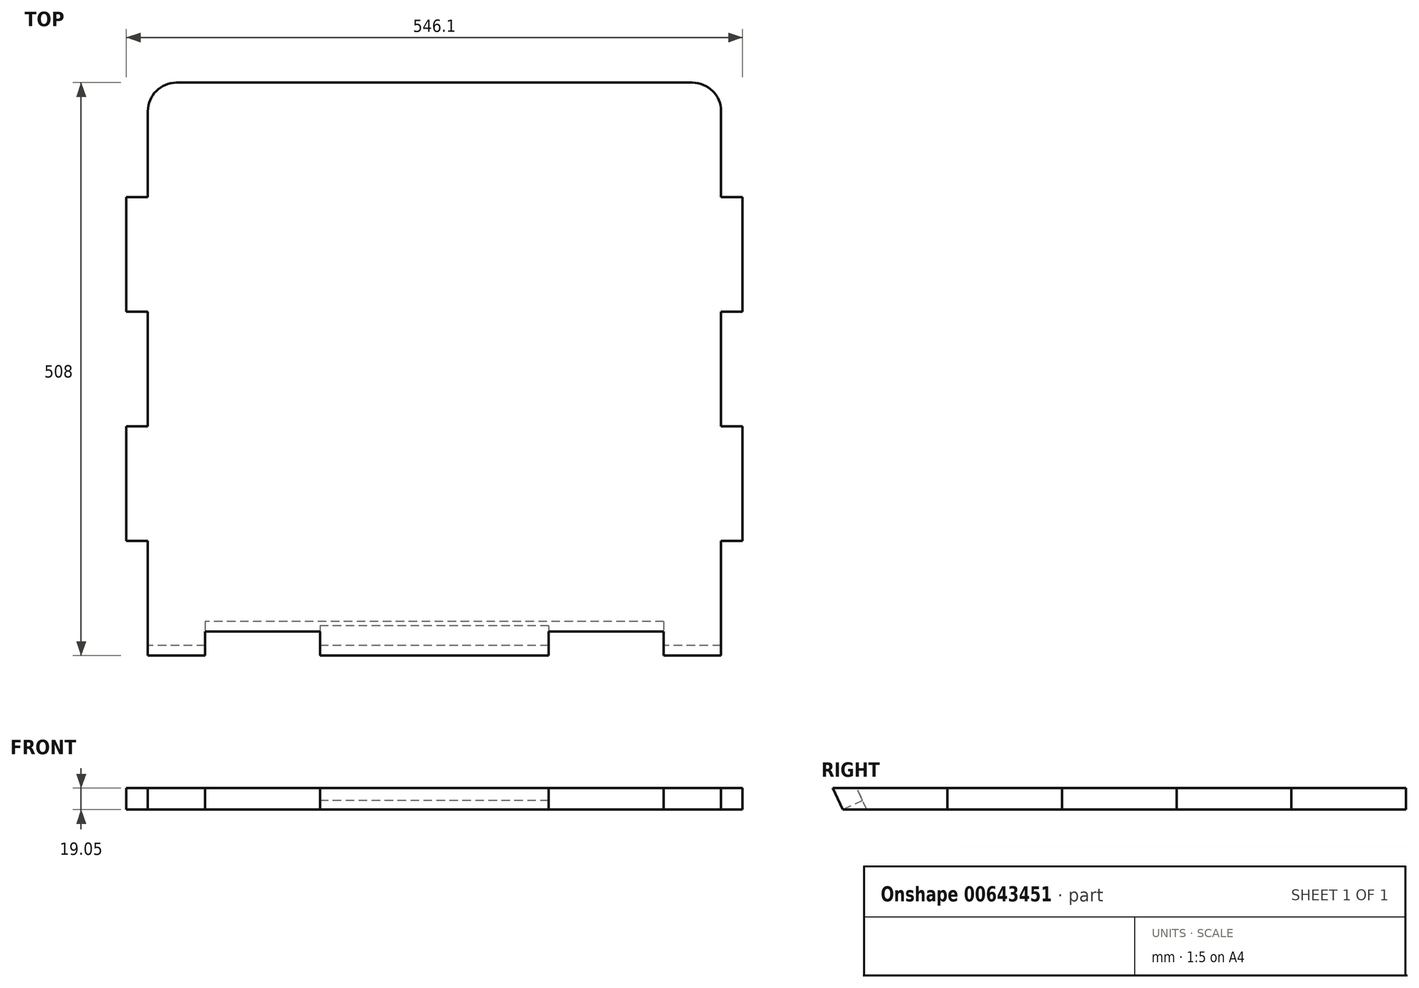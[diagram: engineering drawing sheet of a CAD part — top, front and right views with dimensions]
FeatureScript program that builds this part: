
annotation { "Feature Type Name" : "Feature", "Feature Type Description" : "" }
export const myFeature = defineFeature(function(context is Context, id is Id, definition is map)
    precondition{}
    {
        {
            var Q0;
            Q0=qCreatedBy(makeId("Top.planeOp"),FACE);
            var sketch = newSketch(context, id + "F0", { "sketchPlane" : qUnion([Q0])});
            skLineSegment(sketch, "E0", {"start": v(0, 0) * mm, "end": v(508, 0) * mm});
            skLineSegment(sketch, "E1", {"start": v(254, 0) * mm, "end": v(254, 508) * mm, "construction": true});
            skLineSegment(sketch, "E2", {"start": v(0, 0) * mm, "end": v(0, 101.6) * mm});
            skLineSegment(sketch, "E3", {"start": v(508, 0) * mm, "end": v(508, 101.6) * mm});
            skLineSegment(sketch, "E4", {"start": v(254, 508) * mm, "end": v(508, 508) * mm});
            skLineSegment(sketch, "E5", {"start": v(254, 508) * mm, "end": v(0, 508) * mm});
            skLineSegment(sketch, "E6", {"start": v(254, 254) * mm, "end": v(508, 254) * mm, "construction": true});
            skPoint(sketch, "E6.endSnap0", {"position": v(508, 254) * mm});
            skLineSegment(sketch, "E7", {"start": v(527.05, 355.6) * mm, "end": v(527.05, 406.4) * mm});
            skLineSegment(sketch, "E8", {"start": v(527.05, 406.4) * mm, "end": v(508, 406.4) * mm});
            skLineSegment(sketch, "E9.trimOffspring", {"start": v(508, 406.4) * mm, "end": v(508, 508) * mm});
            skLineSegment(sketch, "E10.MirrorCS", {"start": v(527.05, 355.6) * mm, "end": v(527.05, 304.8) * mm});
            skLineSegment(sketch, "E11.MirrorCS", {"start": v(527.05, 304.8) * mm, "end": v(508, 304.8) * mm});
            skLineSegment(sketch, "E12.MirrorCS", {"start": v(527.05, 101.6) * mm, "end": v(508, 101.6) * mm});
            skLineSegment(sketch, "E13.MirrorCS", {"start": v(527.05, 152.4) * mm, "end": v(527.05, 101.6) * mm});
            skLineSegment(sketch, "E14.MirrorCS", {"start": v(527.05, 152.4) * mm, "end": v(527.05, 203.2) * mm});
            skLineSegment(sketch, "E15.MirrorCS", {"start": v(527.05, 203.2) * mm, "end": v(508, 203.2) * mm});
            skLineSegment(sketch, "E16.trimOffspring", {"start": v(508, 203.2) * mm, "end": v(508, 304.8) * mm});
            skLineSegment(sketch, "E17.MirrorCS", {"start": v(-19.05, 406.4) * mm, "end": v(0, 406.4) * mm});
            skLineSegment(sketch, "E18.MirrorCS", {"start": v(-19.05, 355.6) * mm, "end": v(-19.05, 406.4) * mm});
            skLineSegment(sketch, "E19.MirrorCS", {"start": v(-19.05, 355.6) * mm, "end": v(-19.05, 304.8) * mm});
            skLineSegment(sketch, "E20.MirrorCS", {"start": v(-19.05, 304.8) * mm, "end": v(0, 304.8) * mm});
            skLineSegment(sketch, "E21.MirrorCS", {"start": v(-19.05, 203.2) * mm, "end": v(0, 203.2) * mm});
            skLineSegment(sketch, "E22.MirrorCS", {"start": v(-19.05, 152.4) * mm, "end": v(-19.05, 203.2) * mm});
            skLineSegment(sketch, "E23.MirrorCS", {"start": v(-19.05, 152.4) * mm, "end": v(-19.05, 101.6) * mm});
            skLineSegment(sketch, "E24.MirrorCS", {"start": v(-19.05, 101.6) * mm, "end": v(0, 101.6) * mm});
            skLineSegment(sketch, "E25.trimOffspring", {"start": v(0, 406.4) * mm, "end": v(0, 508) * mm});
            skLineSegment(sketch, "E26.trimOffspring", {"start": v(0, 203.2) * mm, "end": v(0, 304.8) * mm});
            skSolve(sketch);
        }
        {
            var Q0;
            Q0=makeQuery(id+"F0.imprint","IMPRINT",FACE,{"disambiguationData":[TD([[makeQuery(id+"F0.imprint","IMPRINT",EDGE,{"derivedFrom":sQuery(id+"F0.wireOp",EDGE,"E0")}),1.0]])]});
            extrude(context, id + "F1", {"entities" : qUnion([Q0]), "depth" : 19.05 * mm, "offsetDistance" : 25.4 * mm});
        }
        {
            var Q0;
            Q0=makeQuery(id+"F1.opExtrude","SWEPT_EDGE",EDGE,{"disambiguationData":[OSD([sQuery(id+"F0.wireOp",EDGE,"E5"),sQuery(id+"F0.wireOp",EDGE,"E25.trimOffspring")])]});
            var Q1;
            Q1=makeQuery(id+"F1.opExtrude","SWEPT_EDGE",EDGE,{"disambiguationData":[OSD([sQuery(id+"F0.wireOp",EDGE,"E4"),sQuery(id+"F0.wireOp",EDGE,"E9.trimOffspring")])]});
            fillet(context, id + "F2", {"entities" : qUnion([Q0, Q1]), "radius" : 25.4 * mm, "tangentPropagation" : true, "allowEdgeOverflow" : false});
        }
        {
            var Q0;
            Q0=makeQuery(id+"F1.opExtrude","SWEPT_FACE",FACE,{"disambiguationData":[OSD([sQuery(id+"F0.wireOp",EDGE,"E2")])]});
            var sketch = newSketch(context, id + "F3", { "sketchPlane" : qUnion([Q0])});
            skLineSegment(sketch, "E27", {"start": v(0, 19.05) * mm, "end": v(-8.88, 0) * mm});
            skLineSegment(sketch, "E28.0", {"start": v(0, 0) * mm, "end": v(-8.88, 0) * mm});
            skLineSegment(sketch, "E29.0", {"start": v(0, 19.05) * mm, "end": v(0, 0) * mm});
            skPoint(sketch, "E30.orphan", {"position": v(-101.6, 0) * mm});
            skPoint(sketch, "E31.0.end.orphan", {"position": v(-101.6, 19.05) * mm});
            skLineSegment(sketch, "E32.0", {"start": v(0, 19.05) * mm, "end": v(-101.6, 19.05) * mm, "construction": true});
            skSolve(sketch);
        }
        {
            var Q0;
            Q0=makeQuery(id+"F3.imprint","IMPRINT",FACE,{"disambiguationData":[TD([[makeQuery(id+"F3.imprint","IMPRINT",EDGE,{"derivedFrom":sQuery(id+"F3.wireOp",EDGE,"E27")}),1.0]])]});
            extrude(context, id + "F4", {"entities" : qUnion([Q0]), "operationType" : NewBodyOperationType.REMOVE, "endBound" : BoundingType.THROUGH_ALL, "oppositeDirection" : true, "depth" : 25.4 * mm, "offsetDistance" : 25.4 * mm});
        }
        {
            var Q0;
            Q0=makeQuery(id+"F4.boolean.opBoolean","MERGE",EDGE,{"derivedFrom":[makeQuery(id+"F1.opExtrude","CAP_EDGE",EDGE,{"disambiguationData":[OSD([sQuery(id+"F0.wireOp",EDGE,"E0")])],"isStart":false}),makeQuery(id+"F4.opExtrude","SWEPT_EDGE",EDGE,{"disambiguationData":[OSD([sQuery(id+"F0.wireOp",EDGE,"E2"),sQuery(id+"F3.wireOp",EDGE,"E27"),sQuery(id+"F3.wireOp",EDGE,"E29.0")])]})]});
            cPlane(context, id + "F5", {"entities" : qUnion([Q0]), "cplaneType" : CPlaneType.LINE_ANGLE, "offset" : 25.4 * mm, "angle" : 65 * degree, "oppositeDirection" : true, "width" : 152.4 * mm, "height" : 152.4 * mm});
        }
        {
            var Q0;
            Q0=qCreatedBy(id+"F5.planeOp",FACE);
            var sketch = newSketch(context, id + "F6", { "sketchPlane" : qUnion([Q0])});
            skLineSegment(sketch, "E33.0", {"start": v(50.8, -8.05) * mm, "end": v(152.65, -8.05) * mm});
            skLineSegment(sketch, "E34", {"start": v(50.8, -27.33) * mm, "end": v(152.65, -27.33) * mm});
            skLineSegment(sketch, "E35", {"start": v(152.65, -27.33) * mm, "end": v(152.65, -8.05) * mm});
            skLineSegment(sketch, "E36", {"start": v(50.8, -27.33) * mm, "end": v(50.8, -8.05) * mm});
            skLineSegment(sketch, "E37.MirrorCS", {"start": v(355.35, -27.33) * mm, "end": v(355.35, -8.05) * mm});
            skLineSegment(sketch, "E38.MirrorCS", {"start": v(457.2, -27.33) * mm, "end": v(457.2, -8.05) * mm});
            skLineSegment(sketch, "E39.MirrorCS", {"start": v(457.2, -27.33) * mm, "end": v(355.35, -27.33) * mm});
            skPoint(sketch, "E40.start.orphan", {"position": v(0, -8.05) * mm});
            skLineSegment(sketch, "E41.trimOffspring", {"start": v(355.35, -8.05) * mm, "end": v(457.2, -8.05) * mm});
            skPoint(sketch, "E42.orphan", {"position": v(508, -8.05) * mm});
            skPoint(sketch, "E43.start.orphan", {"position": v(254, -8.05) * mm});
            skSolve(sketch);
        }
        {
            var Q0;
            Q0=makeQuery(id+"F6.imprint","IMPRINT",FACE,{"disambiguationData":[TD([[makeQuery(id+"F6.imprint","IMPRINT",EDGE,{"derivedFrom":sQuery(id+"F6.wireOp",EDGE,"E33.0")}),-1.0]])]});
            var Q1;
            Q1=makeQuery(id+"F6.imprint","IMPRINT",FACE,{"disambiguationData":[TD([[makeQuery(id+"F6.imprint","IMPRINT",EDGE,{"derivedFrom":sQuery(id+"F6.wireOp",EDGE,"E37.MirrorCS")}),-1.0]])]});
            extrude(context, id + "F7", {"entities" : qUnion([Q0, Q1]), "operationType" : NewBodyOperationType.REMOVE, "endBound" : BoundingType.THROUGH_ALL, "depth" : 25.4 * mm, "offsetDistance" : 25.4 * mm});
        }
        {
            var Q0;
            Q0=qCreatedBy(id+"F5.planeOp",FACE);
            cPlane(context, id + "F8", {"entities" : qUnion([Q0]), "cplaneType" : CPlaneType.OFFSET, "offset" : 21.03 * mm, "width" : 152.4 * mm, "height" : 152.4 * mm});
        }
        {
            var Q0;
            Q0=qCreatedBy(id+"F8.planeOp",FACE);
            var sketch = newSketch(context, id + "F9", { "sketchPlane" : qUnion([Q0])});
            skLineSegment(sketch, "E44.0", {"start": v(355.35, -27.33) * mm, "end": v(355.35, -8.05) * mm});
            skLineSegment(sketch, "E44.1", {"start": v(355.35, -8.05) * mm, "end": v(152.65, -8.05) * mm});
            skLineSegment(sketch, "E44.2", {"start": v(152.65, -27.33) * mm, "end": v(152.65, -8.05) * mm});
            skLineSegment(sketch, "E45", {"start": v(355.35, -27.33) * mm, "end": v(152.65, -27.33) * mm});
            skSolve(sketch);
        }
        {
            var Q0;
            Q0=qSketchRegion(id+"F9",true);
            extrude(context, id + "F10", {"entities" : qUnion([Q0]), "operationType" : NewBodyOperationType.REMOVE, "endBound" : BoundingType.THROUGH_ALL, "depth" : 25.4 * mm, "offsetDistance" : 25.4 * mm});
        }
    });
